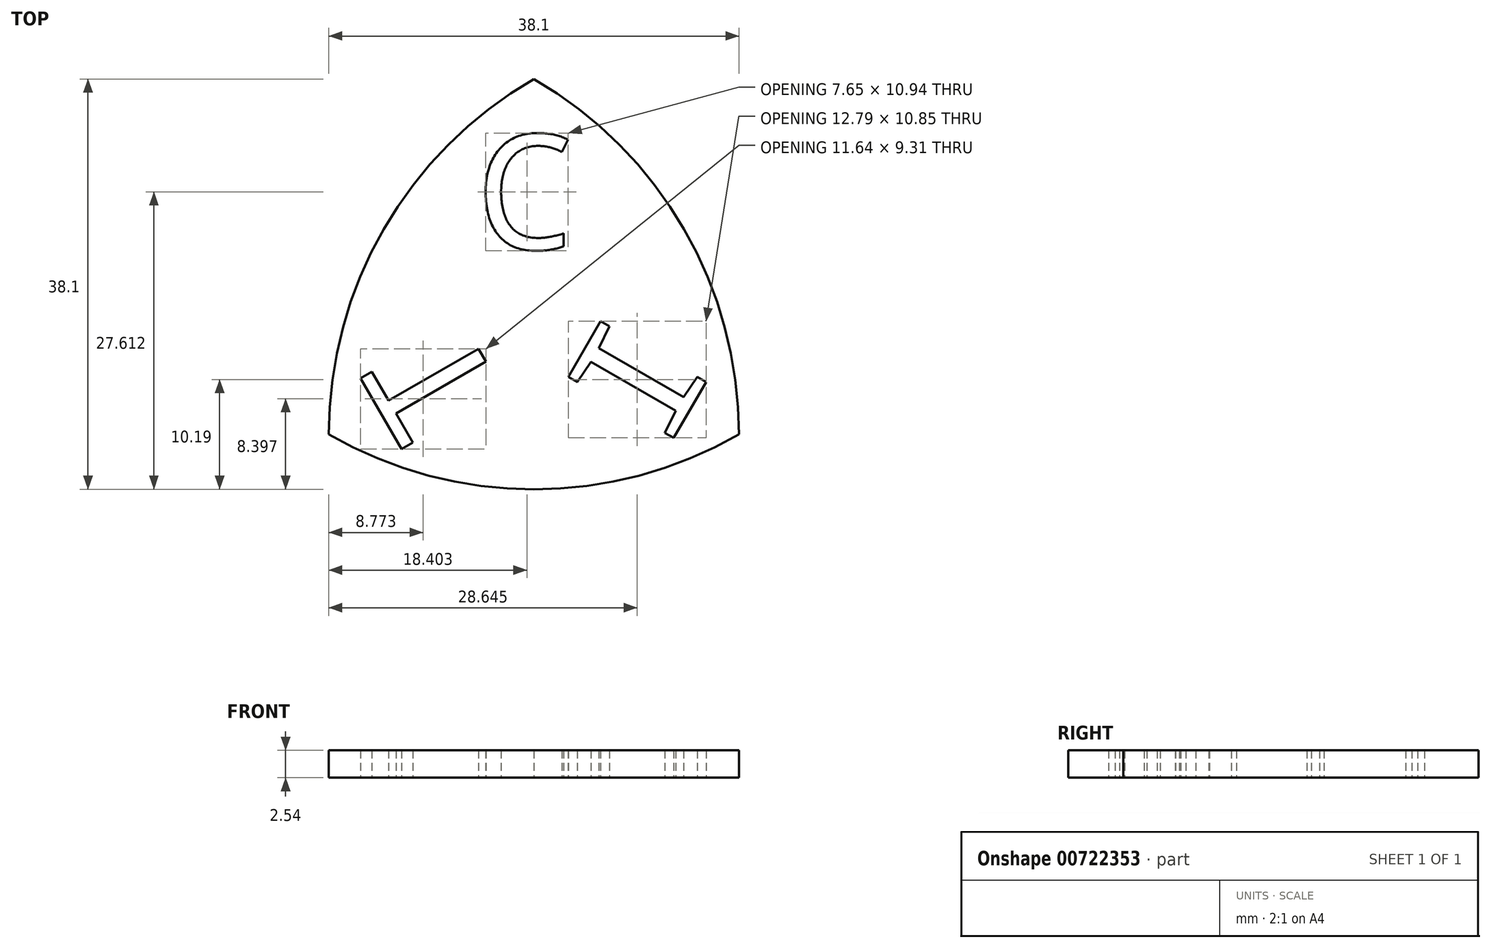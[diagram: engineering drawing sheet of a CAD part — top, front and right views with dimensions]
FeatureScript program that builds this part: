
annotation { "Feature Type Name" : "Feature", "Feature Type Description" : "" }
export const myFeature = defineFeature(function(context is Context, id is Id, definition is map)
    precondition{}
    {
        {
            var Q0;
            Q0=qCreatedBy(makeId("Top.planeOp"),FACE);
            var sketch = newSketch(context, id + "F0", { "sketchPlane" : qUnion([Q0])});
            skCircle(sketch, "E0", {"center": v(0, 0) * mm, "radius": 38.1 * mm});
            skSolve(sketch);
        }
        {
            var Q0;
            Q0=qCreatedBy(makeId("Top.planeOp"),FACE);
            var sketch = newSketch(context, id + "F1", { "sketchPlane" : qUnion([Q0])});
            skCircle(sketch, "E1", {"center": v(-38.1, 0) * mm, "radius": 38.1 * mm});
            skSolve(sketch);
        }
        {
            var Q0;
            Q0=qCreatedBy(makeId("Top.planeOp"),FACE);
            var sketch = newSketch(context, id + "F2", { "sketchPlane" : qUnion([Q0])});
            skCircle(sketch, "E2", {"center": v(-19.05, 33) * mm, "radius": 38.1 * mm});
            skSolve(sketch);
        }
        {
            var Q0;
            Q0=makeQuery(id+"F0.imprint","IMPRINT",FACE,{"disambiguationData":[TD([[makeQuery(id+"F0.imprint","IMPRINT",EDGE,{"derivedFrom":sQuery(id+"F0.wireOp",EDGE,"E0")}),1.0]])]});
            extrude(context, id + "F3", {"entities" : qUnion([Q0]), "depth" : 2.54 * mm, "offsetDistance" : 25.4 * mm});
        }
        {
            var Q0;
            Q0=makeQuery(id+"F2.imprint","IMPRINT",FACE,{"disambiguationData":[TD([[makeQuery(id+"F2.imprint","IMPRINT",EDGE,{"derivedFrom":sQuery(id+"F2.wireOp",EDGE,"E2")}),1.0]])]});
            extrude(context, id + "F4", {"entities" : qUnion([Q0]), "operationType" : NewBodyOperationType.INTERSECT, "depth" : 2.54 * mm, "offsetDistance" : 25.4 * mm});
        }
        {
            var Q0;
            Q0=makeQuery(id+"F1.imprint","IMPRINT",FACE,{"disambiguationData":[TD([[makeQuery(id+"F1.imprint","IMPRINT",EDGE,{"derivedFrom":sQuery(id+"F1.wireOp",EDGE,"E1")}),1.0]])]});
            extrude(context, id + "F5", {"entities" : qUnion([Q0]), "operationType" : NewBodyOperationType.INTERSECT, "depth" : 2.54 * mm, "offsetDistance" : 25.4 * mm});
        }
        {
            var Q0;
            Q0=qCreatedBy(makeId("Top.planeOp"),FACE);
            var sketch = newSketch(context, id + "F6", { "sketchPlane" : qUnion([Q0])});
            skText(sketch, "E3", { "text": "C", "fontName": "DroidSansMono.ttf"});
            skText(sketch, "E4", { "text": "I", "fontName": "DroidSansMono.ttf"});
            skText(sketch, "E5", { "text": "T", "fontName": "DroidSansMono.ttf"});
            const initialGuessF6  = {"E3": [-0.02446, 0.01719, 1, 0, 0.01073], "E4": [-0.00693, -0.00184, 0.5, 0.86603, 0.0114], "E5": [-0.02158, 0.00341, -0.5, 0.86603, 0.01094]};
            skSetInitialGuess(sketch, initialGuessF6);
            skSolve(sketch);
        }
        {
            var Q0;
            Q0 = qSketchRegion(id + "F6", true);
            extrude(context, id + "F7", {"entities" : qUnion([Q0]), "operationType" : NewBodyOperationType.REMOVE, "depth" : 2.54 * mm, "offsetDistance" : 25.4 * mm});
        }
    });
